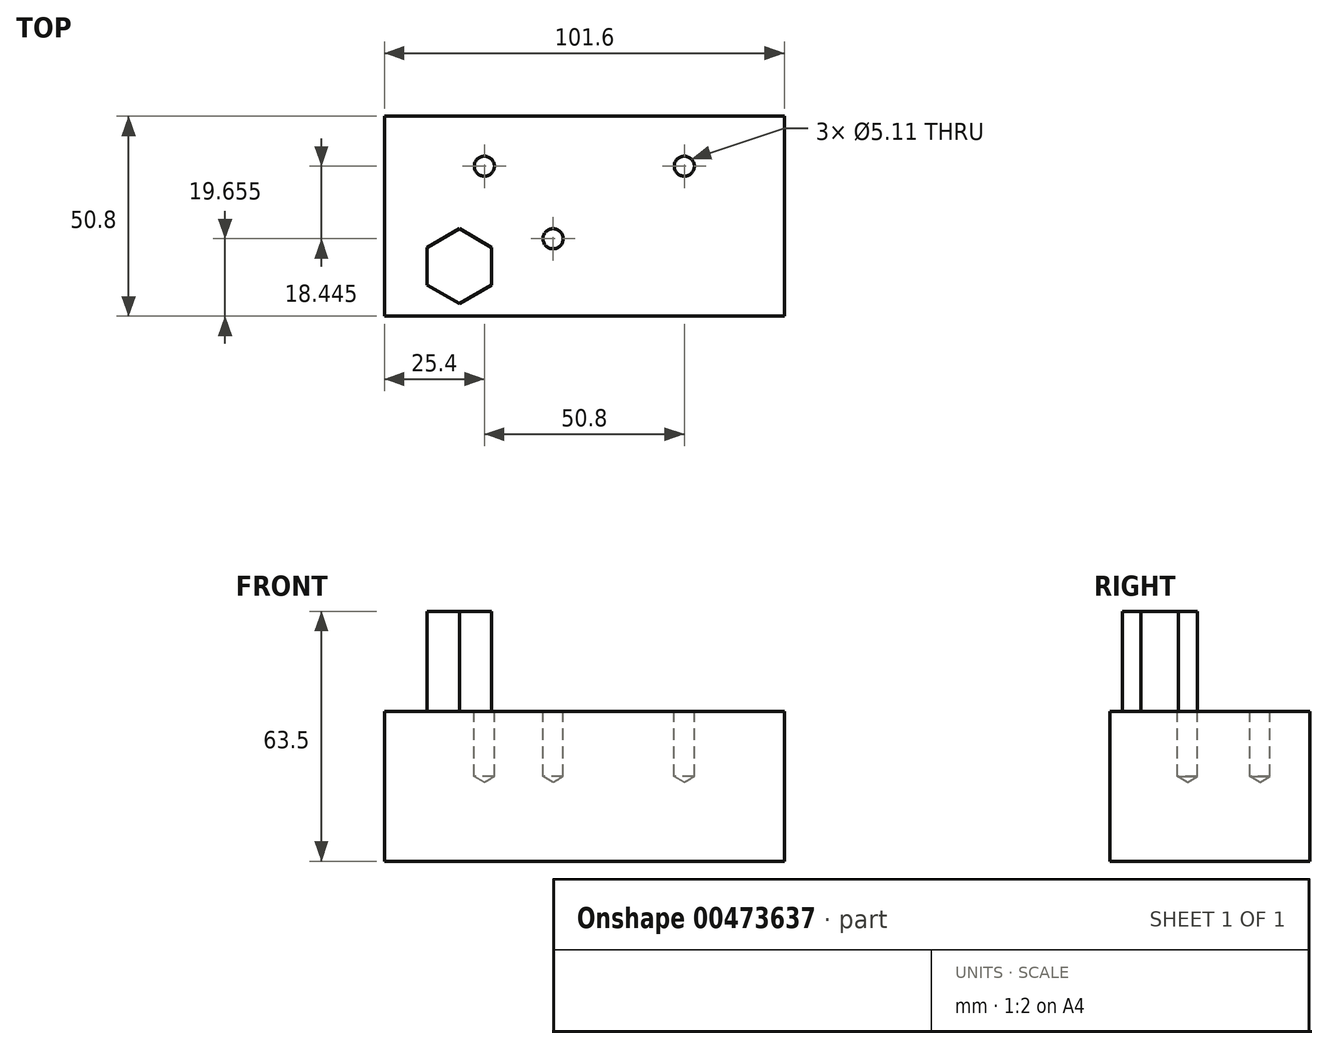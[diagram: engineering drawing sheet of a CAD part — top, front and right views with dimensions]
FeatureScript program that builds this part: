
annotation { "Feature Type Name" : "Feature", "Feature Type Description" : "" }
export const myFeature = defineFeature(function(context is Context, id is Id, definition is map)
    precondition{}
    {
        {
            var Q0;
            Q0=qCreatedBy(makeId("Top.planeOp"),FACE);
            var sketch = newSketch(context, id + "F0", { "sketchPlane" : qUnion([Q0])});
            skLineSegment(sketch, "E0.bottom", {"start": v(0, 0) * mm, "end": v(101.6, 0) * mm});
            skLineSegment(sketch, "E0.top", {"start": v(0, -50.8) * mm, "end": v(101.6, -50.8) * mm});
            skLineSegment(sketch, "E0.left", {"start": v(0, 0) * mm, "end": v(0, -50.8) * mm});
            skLineSegment(sketch, "E0.right", {"start": v(101.6, 0) * mm, "end": v(101.6, -50.8) * mm});
            skSolve(sketch);
        }
        {
            var Q0;
            Q0 = qSketchRegion(id + "F0", true);
            extrude(context, id + "F1", {"entities" : qUnion([Q0]), "depth" : 38.1 * mm});
        }
        {
            var Q0;
            Q0=makeQuery(id+"F1.opExtrude","CAP_FACE",FACE,{"disambiguationData":[OSD([sQuery(id+"F0.wireOp",EDGE,"E0.bottom"),sQuery(id+"F0.wireOp",EDGE,"E0.top"),sQuery(id+"F0.wireOp",EDGE,"E0.left"),sQuery(id+"F0.wireOp",EDGE,"E0.right")])],"isStart":false});
            var sketch = newSketch(context, id + "F2", { "sketchPlane" : qUnion([Q0])});
            skPoint(sketch, "E1", {"position": v(25.4, -12.7) * mm});
            skPoint(sketch, "E2", {"position": v(42.86, -31.15) * mm});
            skPoint(sketch, "E3", {"position": v(76.2, -12.7) * mm});
            skSolve(sketch);
        }
        {
            var Q0;
            Q0=sQuery(id+"F2.wireOp",VERTEX,"E1");
            var Q1;
            Q1=sQuery(id+"F2.wireOp",VERTEX,"E2");
            var Q2;
            Q2=sQuery(id+"F2.wireOp",VERTEX,"E3");
            var Q3;
            Q3=makeQuery(id+"F1.opExtrude","SWEPT_BODY",BODY,{"disambiguationData":[OSD([sQuery(id+"F0.wireOp",EDGE,"E0.bottom"),sQuery(id+"F0.wireOp",EDGE,"E0.top"),sQuery(id+"F0.wireOp",EDGE,"E0.left"),sQuery(id+"F0.wireOp",EDGE,"E0.right")])]});
            hole(context, id + "F3", {"style" : HoleStyle.SIMPLE, "endStyle" : HoleEndStyle.BLIND, "standardTappedOrClearance" : lookupTablePath({ "standard" : "ANSI", "engagement" : "75%", "pitch" : "20 tpi", "size" : "1/4", "type" : "Tapped" }), "standardBlindInLast" : lookupTablePath({ "standard" : "ANSI", "engagement" : "75%", "pitch" : "20 tpi", "size" : "1/4", "type" : "Tapped" }), "holeDiameter" : 5.1 * mm, "showTappedDepth" : true, "holeDepth" : 16.51 * mm, "isTappedThrough" : true, "tappedDepth" : 12.7 * mm, "tapClearance" : 3, "locations" : qUnion([Q0, Q1, Q2]), "scope" : qUnion([Q3]), "majorDiameter" : 6.35 * mm});
        }
        {
            var Q0;
            Q0=makeQuery(id+"F1.opExtrude","CAP_FACE",FACE,{"disambiguationData":[OSD([sQuery(id+"F0.wireOp",EDGE,"E0.bottom"),sQuery(id+"F0.wireOp",EDGE,"E0.top"),sQuery(id+"F0.wireOp",EDGE,"E0.left"),sQuery(id+"F0.wireOp",EDGE,"E0.right")])],"isStart":false});
            var sketch = newSketch(context, id + "F4", { "sketchPlane" : qUnion([Q0])});
            skCircle(sketch, "E4.cCircle", {"center": v(19.05, -38.1) * mm, "radius": 9.53 * mm, "construction": true});
            skLineSegment(sketch, "E4.0", {"start": v(27.3, -42.86) * mm, "end": v(19.05, -47.63) * mm});
            skLineSegment(sketch, "E4.1", {"start": v(19.05, -47.63) * mm, "end": v(10.8, -42.86) * mm});
            skLineSegment(sketch, "E4.2", {"start": v(10.8, -42.86) * mm, "end": v(10.8, -33.34) * mm});
            skLineSegment(sketch, "E4.3", {"start": v(10.8, -33.34) * mm, "end": v(19.05, -28.58) * mm});
            skLineSegment(sketch, "E4.4", {"start": v(19.05, -28.57) * mm, "end": v(27.3, -33.34) * mm});
            skLineSegment(sketch, "E4.5", {"start": v(27.3, -33.34) * mm, "end": v(27.3, -42.86) * mm});
            skSolve(sketch);
        }
        {
            var Q0;
            Q0 = qSketchRegion(id + "F4", true);
            extrude(context, id + "F5", {"entities" : qUnion([Q0]), "operationType" : NewBodyOperationType.ADD, "depth" : 25.4 * mm});
        }
    });
